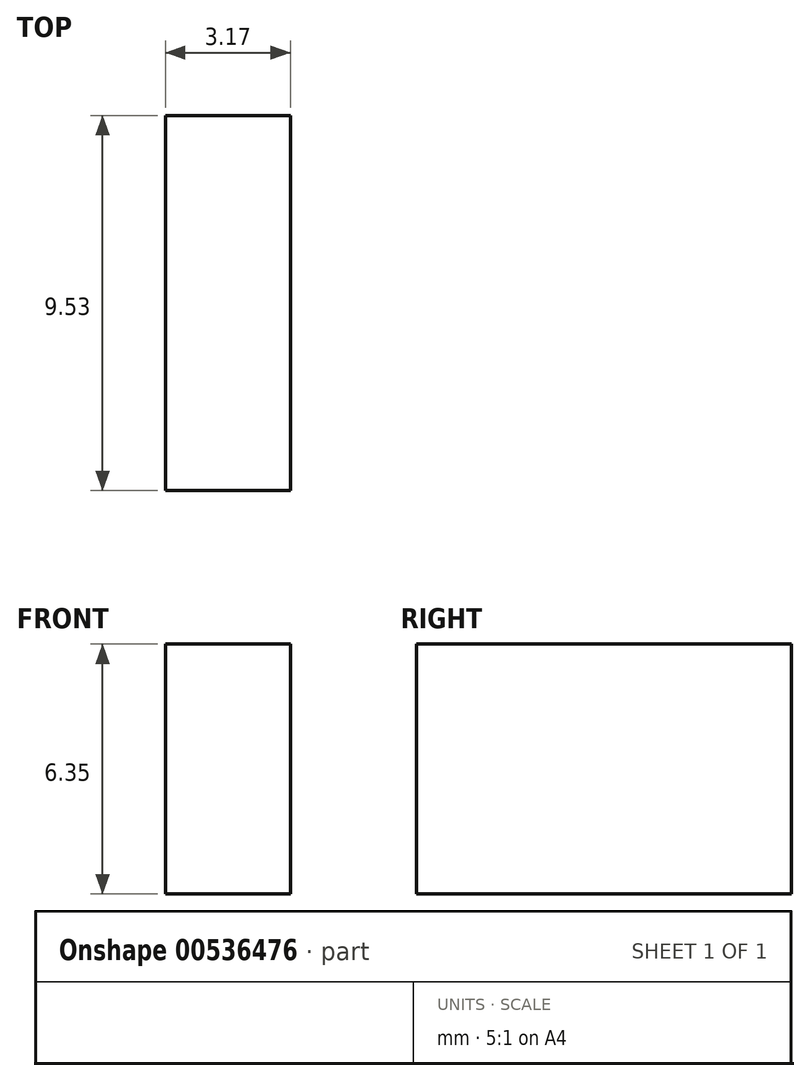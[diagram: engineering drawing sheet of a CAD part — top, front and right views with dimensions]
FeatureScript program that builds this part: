
annotation { "Feature Type Name" : "Feature", "Feature Type Description" : "" }
export const myFeature = defineFeature(function(context is Context, id is Id, definition is map)
    precondition{}
    {
        {
            var Q0;
            Q0=qCreatedBy(makeId("Right.planeOp"), FACE);
            var sketch = newSketch(context, id + "F0", { "sketchPlane" : qUnion([Q0])});
            skLineSegment(sketch, "E0.bottom", {"start": v(0, 0) * mm, "end": v(9.53, 0) * mm});
            skLineSegment(sketch, "E0.top", {"start": v(0, 6.35) * mm, "end": v(9.53, 6.35) * mm});
            skLineSegment(sketch, "E0.left", {"start": v(0, 0) * mm, "end": v(0, 6.35) * mm});
            skLineSegment(sketch, "E0.right", {"start": v(9.53, 0) * mm, "end": v(9.53, 6.35) * mm});
            skSolve(sketch);
        }
        {
            var Q0;
            Q0 = qSketchRegion(id + "F0", true);
            extrude(context, id + "F1", {"entities" : qUnion([Q0]), "depth" : 3.17 * mm, "offsetDistance" : 25.4 * mm});
        }
    });
